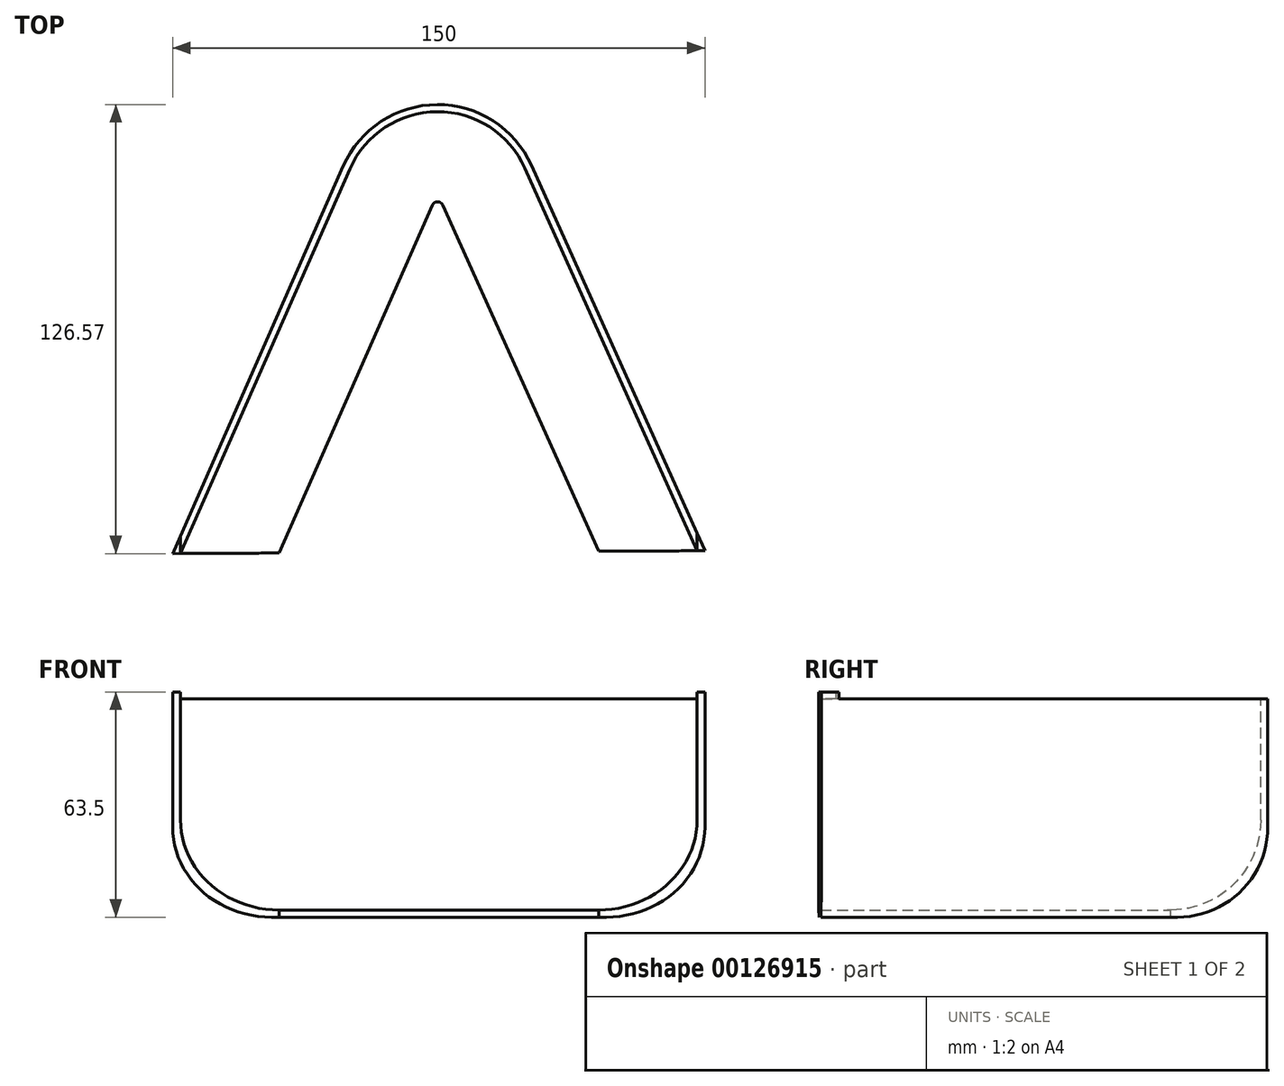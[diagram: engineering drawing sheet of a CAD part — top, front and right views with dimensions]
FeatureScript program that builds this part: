
annotation { "Feature Type Name" : "Feature", "Feature Type Description" : "" }
export const myFeature = defineFeature(function(context is Context, id is Id, definition is map)
    precondition{}
    {
        {
            var Q0;
            Q0=qCreatedBy(makeId("Top.planeOp"),FACE);
            var sketch = newSketch(context, id + "F0", { "sketchPlane" : qUnion([Q0])});
            skLineSegment(sketch, "E0", {"start": v(-58.27, -54.48) * mm, "end": v(91.73, -54.48) * mm});
            skLineSegment(sketch, "E1", {"start": v(91.73, -54.48) * mm, "end": v(91.73, 34.42) * mm});
            skLineSegment(sketch, "E2", {"start": v(-58.27, -54.48) * mm, "end": v(-58.27, 33.98) * mm});
            skLineSegment(sketch, "E3", {"start": v(-12.86, 131.36) * mm, "end": v(-12.86, 131.36) * mm});
            skCircle(sketch, "E4", {"center": v(16.27, 131.36) * mm, "radius": 29.01 * mm});
            skLineSegment(sketch, "E5", {"start": v(-58.27, 33.98) * mm, "end": v(91.73, 34.42) * mm});
            skLineSegment(sketch, "E6", {"start": v(45.4, 131.36) * mm, "end": v(45.28, 131.88) * mm});
            skLineSegment(sketch, "E7", {"start": v(-12.86, 131.36) * mm, "end": v(45.4, 131.36) * mm});
            skLineSegment(sketch, "E8", {"start": v(91.73, 34.42) * mm, "end": v(42.73, 143.27) * mm});
            skLineSegment(sketch, "E9", {"start": v(-58.27, 33.98) * mm, "end": v(-10.29, 143.05) * mm});
            skSolve(sketch);
        }
        {
            var Q0;
            {var subQ8=sQuery(id+"F0.wireOp",EDGE,"E5");Q0=makeQuery(id+"F0.imprint","IMPRINT",FACE,{"disambiguationData":[TD([[makeQuery(id+"F0.imprint","IMPRINT",EDGE,{"derivedFrom":subQ8}),1.0]])]});}
            var Q1;
            {var subQ0=sQuery(id+"F0.wireOp",EDGE,"E4");var subQ1=sQuery(id+"F0.wireOp",EDGE,"E3");var subQ2=makeQuery(id+"F0.imprint","INTERSECT",VERTEX,{"disambiguationData":[OD(0.0)],"derivedFrom":[subQ1,subQ0]});Q1=makeQuery(id+"F0.imprint","IMPRINT",FACE,{"disambiguationData":[TD([[makeQuery(id+"F0.imprint","IMPRINT",EDGE,{"disambiguationData":[TD([[subQ2,-1.0]])],"derivedFrom":subQ1}),-1.0]])]});}
            var Q2;
            {var subQ0=sQuery(id+"F0.wireOp",EDGE,"E4");var subQ1=sQuery(id+"F0.wireOp",EDGE,"E3");var subQ2=makeQuery(id+"F0.imprint","INTERSECT",VERTEX,{"disambiguationData":[OD(0.0)],"derivedFrom":[subQ1,subQ0]});Q2=makeQuery(id+"F0.imprint","IMPRINT",FACE,{"disambiguationData":[TD([[makeQuery(id+"F0.imprint","IMPRINT",EDGE,{"disambiguationData":[TD([[subQ2,-1.0]])],"derivedFrom":subQ1}),1.0]])]});}
            var Q3;
            {var subQ0=sQuery(id+"F0.wireOp",EDGE,"E4");var subQ1=sQuery(id+"F0.wireOp",EDGE,"D9Wxpcgx-FRDK-DbLZ-iwdj-hQiKzaASWyzm");var subQ2=makeQuery(id+"F0.imprint","INTERSECT",VERTEX,{"derivedFrom":[subQ1,subQ0]});Q3=makeQuery(id+"F0.imprint","IMPRINT",FACE,{"disambiguationData":[TD([[makeQuery(id+"F0.imprint","IMPRINT",EDGE,{"disambiguationData":[TD([[subQ2,1.0]])],"derivedFrom":subQ1}),1.0]])]});}
            var Q4;
            {var subQ0=sQuery(id+"F0.wireOp",EDGE,"E4");var subQ1=sQuery(id+"F0.wireOp",EDGE,"HcY7w5fG-ahRs-SSt2-w42w-nCKooS3vVB2g");var subQ2=makeQuery(id+"F0.imprint","INTERSECT",VERTEX,{"derivedFrom":[subQ1,subQ0]});Q4=makeQuery(id+"F0.imprint","IMPRINT",FACE,{"disambiguationData":[TD([[makeQuery(id+"F0.imprint","IMPRINT",EDGE,{"disambiguationData":[TD([[subQ2,1.0]])],"derivedFrom":subQ1}),-1.0]])]});}
            var Q5;
            {var subQ0=sQuery(id+"F0.wireOp",EDGE,"E4");var subQ1=makeQuery(id+"F0.imprint","INTERSECT",VERTEX,{"derivedFrom":[subQ0,sQuery(id+"F0.wireOp",EDGE,"E6")]});Q5=makeQuery(id+"F0.imprint","IMPRINT",FACE,{"disambiguationData":[TD([[makeQuery(id+"F0.imprint","IMPRINT",EDGE,{"disambiguationData":[TD([[subQ1,1.0]])],"derivedFrom":subQ0}),1.0]])]});}
            var Q6;
            {var subQ0=sQuery(id+"F0.wireOp",EDGE,"E7");var subQ1=sQuery(id+"F0.wireOp",EDGE,"E4");var subQ2=makeQuery(id+"F0.imprint","INTERSECT",VERTEX,{"disambiguationData":[OD(0.0)],"derivedFrom":[subQ1,subQ0]});Q6=makeQuery(id+"F0.imprint","IMPRINT",FACE,{"disambiguationData":[TD([[makeQuery(id+"F0.imprint","IMPRINT",EDGE,{"disambiguationData":[TD([[subQ2,1.0]])],"derivedFrom":subQ1}),1.0]])]});}
            var Q7;
            {var subQ0=sQuery(id+"F0.wireOp",EDGE,"E6");Q7=makeQuery(id+"F0.imprint","IMPRINT",FACE,{"disambiguationData":[TD([[makeQuery(id+"F0.imprint","IMPRINT",EDGE,{"derivedFrom":subQ0}),1.0]])]});}
            var Q8;
            {var subQ0=sQuery(id+"F0.wireOp",EDGE,"172b273b-9b99-4067-9b8f-42eab458cd90");Q8=makeQuery(id+"F0.imprint","IMPRINT",FACE,{"disambiguationData":[TD([[makeQuery(id+"F0.imprint","IMPRINT",EDGE,{"derivedFrom":subQ0}),-1.0]])]});}
            var Q9;
            {var subQ0=sQuery(id+"F0.wireOp",EDGE,"qGNRiSTc-UIiT-TgPT-rU2n-yPBoxvX3BfhF");Q9=makeQuery(id+"F0.imprint","IMPRINT",FACE,{"disambiguationData":[TD([[makeQuery(id+"F0.imprint","IMPRINT",EDGE,{"derivedFrom":subQ0}),-1.0]])]});}
            var Q10;
            {var subQ0=sQuery(id+"F0.wireOp",EDGE,"E7");var subQ1=sQuery(id+"F0.wireOp",EDGE,"E4");var subQ2=makeQuery(id+"F0.imprint","INTERSECT",VERTEX,{"disambiguationData":[OD(0.0)],"derivedFrom":[subQ1,subQ0]});Q10=makeQuery(id+"F0.imprint","IMPRINT",FACE,{"disambiguationData":[TD([[makeQuery(id+"F0.imprint","IMPRINT",EDGE,{"disambiguationData":[TD([[subQ2,-1.0]])],"derivedFrom":subQ1}),1.0]])]});}
            extrude(context, id + "F1", {"entities" : qUnion([Q0, Q1, Q2, Q3, Q4, Q5, Q6, Q7, Q8, Q9, Q10]), "depth" : 63.5 * mm});
        }
        {
            var Q0;
            Q0=makeQuery(id+"F1.opExtrude","SWEPT_FACE",FACE,{"disambiguationData":[OSD([sQuery(id+"F0.wireOp",EDGE,"E5")])]});
            var Q1;
            Q1=makeQuery(id+"F1.opExtrude","SWEPT_BODY",BODY,{"disambiguationData":[OSD([sQuery(id+"F0.wireOp",EDGE,"E0"),sQuery(id+"F0.wireOp",EDGE,"E1"),sQuery(id+"F0.wireOp",EDGE,"E2"),sQuery(id+"F0.wireOp",EDGE,"HcY7w5fG-ahRs-SSt2-w42w-nCKooS3vVB2g"),sQuery(id+"F0.wireOp",EDGE,"D9Wxpcgx-FRDK-DbLZ-iwdj-hQiKzaASWyzm"),sQuery(id+"F0.wireOp",EDGE,"E4")])]});
            shell(context, id + "F2", {"entities" : qUnion([Q0]), "parts" : qUnion([Q1]), "thickness" : 2 * mm});
        }
        {
            var Q0;
            Q0=makeQuery(id+"F1.opExtrude","CAP_EDGE",EDGE,{"disambiguationData":[OSD([sQuery(id+"F0.wireOp",EDGE,"E4")])],"isStart":false});
            var Q1;
            {var subQ0=sQuery(id+"F0.wireOp",EDGE,"E4");Q1=makeQuery(id+"F2.opShell","OFFSET_EDGE",EDGE,{"disambiguationData":[OSD([subQ0]),TDD([makeQuery(id+"F1.opExtrude","CAP_EDGE",EDGE,{"disambiguationData":[OSD([subQ0])],"isStart":false})])]});}
            fillet(context, id + "F3", {"entities" : qUnion([Q0, Q1]), "radius" : 25.4 * mm, "tangentPropagation" : true, "allowEdgeOverflow" : false});
        }
        {
            var Q0;
            Q0=makeQuery(id+"F1.opExtrude","SWEPT_BODY",BODY,{"disambiguationData":[OSD([sQuery(id+"F0.wireOp",EDGE,"E4"),sQuery(id+"F0.wireOp",EDGE,"E5"),sQuery(id+"F0.wireOp",EDGE,"E8"),sQuery(id+"F0.wireOp",EDGE,"E9")])]});
            var Q1;
            {var subQ0=sQuery(id+"F0.wireOp",EDGE,"E8");Q1=makeQuery(id+"F3.opFillet","BLEND_EDGE",EDGE,{"blendedFrom":[makeQuery(id+"F1.opExtrude","CAP_EDGE",EDGE,{"disambiguationData":[OSD([subQ0])],"isStart":false}),makeQuery(id+"F1.opExtrude","CAP_FACE",FACE,{"disambiguationData":[OSD([sQuery(id+"F0.wireOp",EDGE,"E4"),sQuery(id+"F0.wireOp",EDGE,"E5"),subQ0,sQuery(id+"F0.wireOp",EDGE,"E9")])],"isStart":false})],"blendedInto":[makeQuery(id+"F1.opExtrude","CAP_FACE",FACE,{"disambiguationData":[OSD([sQuery(id+"F0.wireOp",EDGE,"E4"),sQuery(id+"F0.wireOp",EDGE,"E5"),subQ0,sQuery(id+"F0.wireOp",EDGE,"E9")])],"isStart":false})]});}
            transform(context, id + "F4", {"entities" : qUnion([Q0]), "transformType" : TransformType.ROTATION, "transformAxis" : qUnion([Q1]), "angle" : 180 * degree, "makeCopy" : false});
        }
        {
            var Q0;
            Q0=makeQuery(id+"F1.opExtrude","SWEPT_BODY",BODY,{"disambiguationData":[OSD([sQuery(id+"F0.wireOp",EDGE,"E4"),sQuery(id+"F0.wireOp",EDGE,"E5"),sQuery(id+"F0.wireOp",EDGE,"E8"),sQuery(id+"F0.wireOp",EDGE,"E9")])]});
            var Q1;
            Q1=qCreatedBy(makeId("Origin.pointOp"),VERTEX);
            var Q2;
            {var subQ0=sQuery(id+"F0.wireOp",EDGE,"E9");var subQ1=sQuery(id+"F0.wireOp",EDGE,"E8");var subQ2=sQuery(id+"F0.wireOp",EDGE,"E5");var subQ3=sQuery(id+"F0.wireOp",EDGE,"E4");Q2=makeQuery(id+"F3.opFillet","BLEND_EDGE",EDGE,{"blendedFrom":[makeQuery(id+"F2.opShell","OFFSET_EDGE",EDGE,{"disambiguationData":[OSD([subQ1]),TDD([makeQuery(id+"F1.opExtrude","CAP_EDGE",EDGE,{"disambiguationData":[OSD([subQ1])],"isStart":false})])]}),makeQuery(id+"F2.opShell","OFFSET_FACE",FACE,{"disambiguationData":[OSD([subQ3,subQ2,subQ1,subQ0]),TDD([makeQuery(id+"F1.opExtrude","CAP_FACE",FACE,{"disambiguationData":[OSD([subQ3,subQ2,subQ1,subQ0])],"isStart":false})])]})],"blendedInto":[makeQuery(id+"F2.opShell","OFFSET_FACE",FACE,{"disambiguationData":[OSD([subQ3,subQ2,subQ1,subQ0]),TDD([makeQuery(id+"F1.opExtrude","CAP_FACE",FACE,{"disambiguationData":[OSD([subQ3,subQ2,subQ1,subQ0])],"isStart":false})])]})]});}
            var Q3;
            Q3=makeQuery(id+"F1.opExtrude","SWEPT_EDGE",EDGE,{"disambiguationData":[OSD([sQuery(id+"F0.wireOp",EDGE,"E1"),sQuery(id+"F0.wireOp",EDGE,"E5"),sQuery(id+"F0.wireOp",EDGE,"E8")])]});
            transform(context, id + "F5", {"entities" : qUnion([Q0]), "transformType" : TransformType.ROTATION, "transformAxis" : qUnion([Q3]), "angle" : 48 * degree, "oppositeDirection" : true, "makeCopy" : false});
        }
        {
            var Q0;
            Q0=makeQuery(id+"F1.opExtrude","SWEPT_FACE",FACE,{"disambiguationData":[OSD([sQuery(id+"F0.wireOp",EDGE,"E5")])]});
            var sketch = newSketch(context, id + "F6", { "sketchPlane" : qUnion([Q0])});
            skLineSegment(sketch, "E10", {"start": v(47.67, 125) * mm, "end": v(193.3, 125) * mm});
            skLineSegment(sketch, "E11", {"start": v(193.3, 125) * mm, "end": v(193.3, 127) * mm});
            skLineSegment(sketch, "E12", {"start": v(193.3, 127) * mm, "end": v(47.67, 127) * mm});
            skLineSegment(sketch, "E13", {"start": v(47.67, 127) * mm, "end": v(47.67, 125) * mm});
            skSolve(sketch);
        }
        {
            var Q0;
            Q0 = qSketchRegion(id + "F6", true);
            extrude(context, id + "F7", {"entities" : qUnion([Q0]), "operationType" : NewBodyOperationType.REMOVE, "oppositeDirection" : true, "depth" : 127 * mm});
        }
        {
            var Q0;
            {var subQ0=sQuery(id+"F0.wireOp",EDGE,"E9");var subQ1=sQuery(id+"F0.wireOp",EDGE,"E8");var subQ2=sQuery(id+"F0.wireOp",EDGE,"E5");var subQ3=sQuery(id+"F0.wireOp",EDGE,"E4");Q0=makeQuery(id+"F2.opShell","OFFSET_FACE",FACE,{"disambiguationData":[OSD([subQ3,subQ2,subQ1,subQ0]),TDD([makeQuery(id+"F1.opExtrude","CAP_FACE",FACE,{"disambiguationData":[OSD([subQ3,subQ2,subQ1,subQ0])],"isStart":false})])]});}
            extrude(context, id + "F8", {"entities" : qUnion([Q0]), "operationType" : NewBodyOperationType.REMOVE, "oppositeDirection" : true, "depth" : 25.4 * mm});
        }
    });
